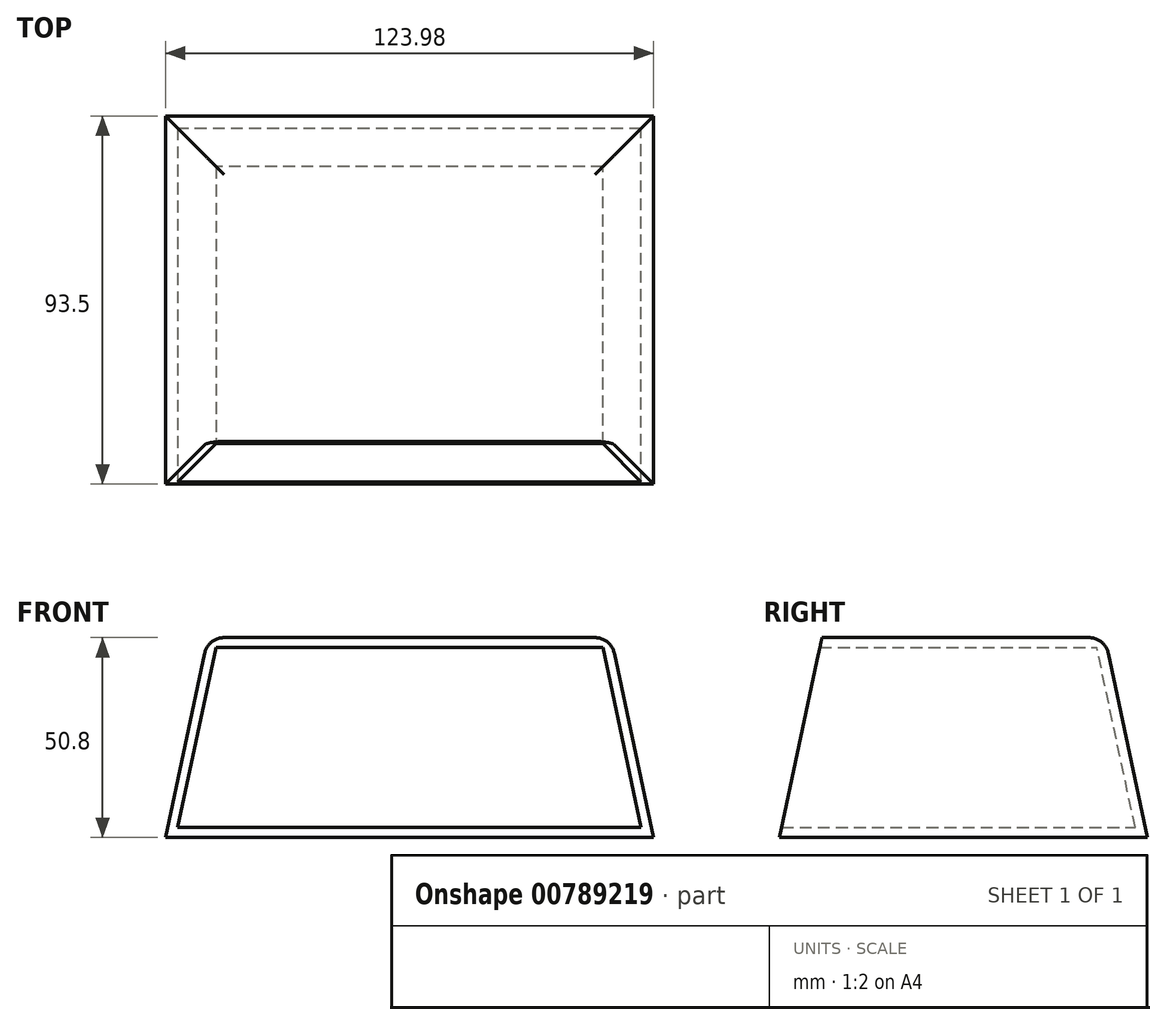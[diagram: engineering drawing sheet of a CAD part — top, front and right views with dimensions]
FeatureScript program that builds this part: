
annotation { "Feature Type Name" : "Feature", "Feature Type Description" : "" }
export const myFeature = defineFeature(function(context is Context, id is Id, definition is map)
    precondition{}
    {
        {
            var Q0;
            Q0=qCreatedBy(makeId("Top.planeOp"),FACE);
            var sketch = newSketch(context, id + "F0", { "sketchPlane" : qUnion([Q0])});
            skLineSegment(sketch, "E0.bottom", {"start": v(51.19, -35.95) * mm, "end": v(-51.19, -35.95) * mm});
            skLineSegment(sketch, "E0.top", {"start": v(51.19, 35.95) * mm, "end": v(-51.19, 35.95) * mm});
            skLineSegment(sketch, "E0.left", {"start": v(51.19, -35.95) * mm, "end": v(51.19, 35.95) * mm});
            skLineSegment(sketch, "E0.right", {"start": v(-51.19, -35.95) * mm, "end": v(-51.19, 35.95) * mm});
            skPoint(sketch, "E0.middle", {"position": v(0, 0) * mm});
            skSolve(sketch);
        }
        {
            var Q0;
            Q0=makeQuery(id+"F0.imprint","IMPRINT",FACE,{"disambiguationData":[TD([[makeQuery(id+"F0.imprint","IMPRINT",EDGE,{"derivedFrom":sQuery(id+"F0.wireOp",EDGE,"E0.bottom")}),-1.0]])]});
            extrude(context, id + "F1", {"entities" : qUnion([Q0]), "oppositeDirection" : true, "depth" : 50.8 * mm, "offsetDistance" : 25.4 * mm, "hasDraft" : true, "draftAngle" : 12 * degree});
        }
        {
            var Q0;
            Q0=makeQuery(id+"F1.opExtrude","SWEPT_FACE",FACE,{"disambiguationData":[OSD([sQuery(id+"F0.wireOp",EDGE,"E0.bottom")])]});
            shell(context, id + "F2", {"entities" : qUnion([Q0]), "thickness" : 2.54 * mm});
        }
        {
            var Q0;
            Q0=makeQuery(id+"F1.opExtrude","CAP_EDGE",EDGE,{"disambiguationData":[OSD([sQuery(id+"F0.wireOp",EDGE,"E0.left")])],"isStart":true});
            var Q1;
            Q1=makeQuery(id+"F1.opExtrude","CAP_EDGE",EDGE,{"disambiguationData":[OSD([sQuery(id+"F0.wireOp",EDGE,"E0.right")])],"isStart":true});
            var Q2;
            Q2=makeQuery(id+"F1.opExtrude","CAP_EDGE",EDGE,{"disambiguationData":[OSD([sQuery(id+"F0.wireOp",EDGE,"E0.top")])],"isStart":true});
            fillet(context, id + "F3", {"entities" : qUnion([Q0, Q1, Q2]), "radius" : 5.08 * mm, "tangentPropagation" : true, "allowEdgeOverflow" : false});
        }
    });
